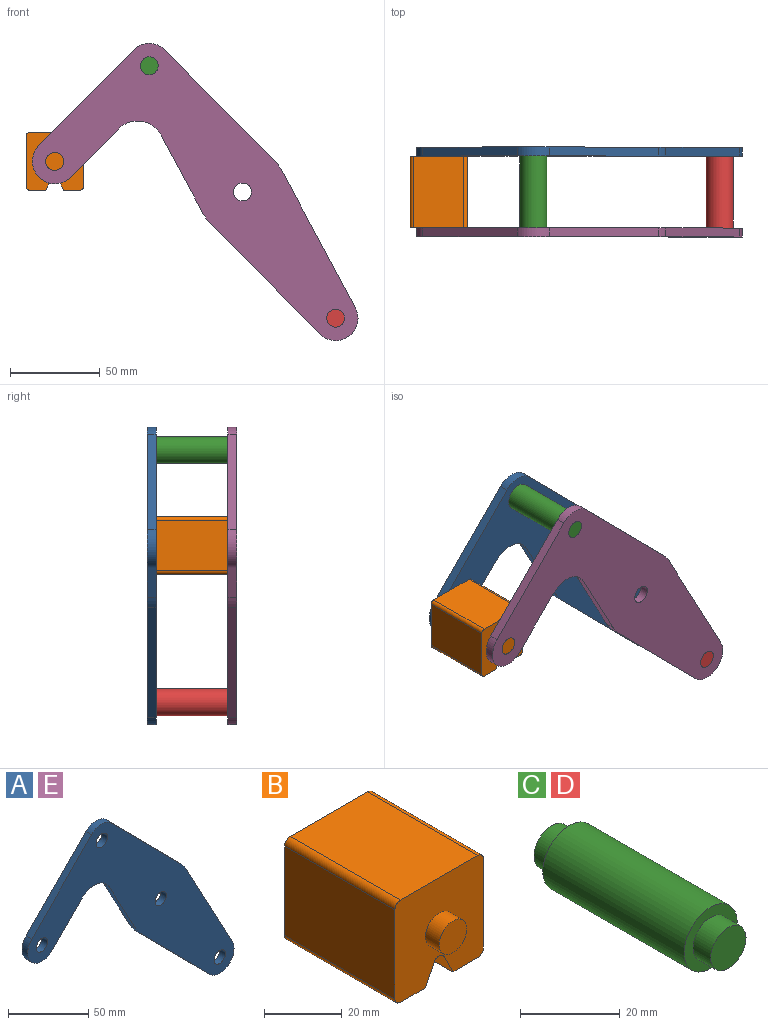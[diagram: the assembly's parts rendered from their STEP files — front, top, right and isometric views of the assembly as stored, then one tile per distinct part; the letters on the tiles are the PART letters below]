
ASSEMBLY  parts=5 mates=3
PART A: 18 faces, bbox 181.7x5x165.8 mm
  f0: plane 43.49x23.35mm, normal (-0.88,0,-0.47), area 246.8mm2, adj f1,f14,f16,f17
  f1: cylinder r=25mm len=5.75mm, axis (0,1,0), area 35.8mm2, adj f0,f2,f16,f17
  f2: plane 61.6x60.87mm, normal (-0.71,0,-0.7), area 433mm2, adj f1,f3,f16,f17
  f3: cylinder r=12.5mm len=21.39mm, axis (0,1,0), area 178.4mm2, adj f2,f4,f16,f17
  f4: plane 76.3x40.96mm, normal (0.88,0,0.47), area 433mm2, adj f3,f5,f16,f17
  f5: cylinder r=25mm len=5.75mm, axis (0,1,0), area 35.8mm2, adj f4,f6,f16,f17
  f6: plane 61.6x60.87mm, normal (0.71,0,0.7), area 433mm2, adj f5,f7,f16,f17
  f7: cylinder r=12.5mm len=17.78mm, axis (0,1,0), area 98.9mm2, adj f6,f8,f16,f17
  f8: plane 53.35x52.71mm, normal (-0.71,0,0.7), area 375mm2, adj f7,f9,f16,f17
  f9: cylinder r=12.5mm len=21.39mm, axis (0,1,0), area 196.3mm2, adj f8,f10,f16,f17
  f10: plane 26.86x26.54mm, normal (0.71,0,-0.7), area 188.8mm2, adj f9,f14,f16,f17
  f11: cylinder r=5mm len=10mm, axis (0,1,0), area 157.1mm2, adj f16,f17
  f12: cylinder r=5mm len=10mm, axis (0,1,0), area 157.1mm2, adj f16,f17
  f13: cylinder r=5mm len=10mm, axis (0,1,0), area 157.1mm2, adj f16,f17
  f14: cylinder r=15mm len=23.89mm, axis (0,1,0), area 140.2mm2, adj f0,f10,f16,f17
  f15: cylinder r=5mm len=10mm, axis (0,1,0), area 157.1mm2, adj f16,f17
  f16: plane 181.66x165.78mm, normal (0,-1,0), area 8710.1mm2, adj f0,f1,f2,f3,f4,f5,f6,f7
  f17: plane 181.66x165.78mm, normal (0,1,0), area 8710.1mm2, adj f0,f1,f2,f3,f4,f5,f6,f7
PART B: 18 faces, bbox 32.1x50x32.1 mm
  f0: plane 40x28.08mm, normal (1,0,0), area 1123.1mm2, adj f4,f10,f13,f14
  f1: plane 40x9.04mm, normal (0,0,-1), area 361.6mm2, adj f2,f4,f10,f14
  f2: plane 40x6.42mm, normal (-0.89,0,-0.45), area 287.2mm2, adj f1,f4,f10,f15
  f3: plane 40x6.42mm, normal (0.89,0,-0.45), area 287.2mm2, adj f4,f5,f10,f15
  f4: plane 32.08x32.08mm, normal (0,-1,0), area 900.6mm2, adj f0,f1,f2,f3,f5,f6,f7,f9
  f5: plane 40x9.04mm, normal (0,0,-1), area 361.6mm2, adj f3,f4,f10,f16
  f6: plane 40x28.08mm, normal (0,0,1), area 1123.1mm2, adj f4,f10,f13,f17
  f7: plane 40x28.08mm, normal (-1,0,0), area 1123.1mm2, adj f4,f10,f16,f17
  f8: plane 10x10mm, normal (0,-1,0), area 78.5mm2, adj f9
  f9: cylinder r=5mm len=10mm, axis (0,1,0), area 157.1mm2, adj f4,f8
  f10: plane 32.08x32.08mm, normal (0,1,0), area 900.6mm2, adj f0,f1,f2,f3,f5,f6,f7,f12
  f11: plane 10x10mm, normal (0,1,0), area 78.5mm2, adj f12
  f12: cylinder r=5mm len=10mm, axis (0,-1,0), area 157.1mm2, adj f10,f11
  f13: cylinder r=2mm len=40mm, axis (0,1,0), area 125.7mm2, adj f0,f4,f6,f10
  f14: cylinder r=2mm len=40mm, axis (0,-1,0), area 125.7mm2, adj f0,f1,f4,f10
  f15: cylinder r=2mm len=40mm, axis (0,1,0), area 177.1mm2, adj f2,f3,f4,f10
  f16: cylinder r=2mm len=40mm, axis (0,1,0), area 125.7mm2, adj f4,f5,f7,f10
  f17: cylinder r=2mm len=40mm, axis (0,-1,0), area 125.7mm2, adj f4,f6,f7,f10
PART C: 7 faces, bbox 15x50x15 mm
  f0: cylinder r=7.5mm len=40mm, axis (0,-1,0), area 1885mm2, adj f2,f5
  f1: cylinder r=5mm len=10mm, axis (0,1,0), area 157.1mm2, adj f2,f3
  f2: plane 15x15mm, normal (0,-1,0), area 98.2mm2, adj f0,f1
  f3: plane 10x10mm, normal (0,-1,0), area 78.5mm2, adj f1
  f4: cylinder r=5mm len=10mm, axis (0,-1,0), area 157.1mm2, adj f5,f6
  f5: plane 15x15mm, normal (0,1,0), area 98.2mm2, adj f0,f4
  f6: plane 10x10mm, normal (0,1,0), area 78.5mm2, adj f4
PART D: same geometry as C
PART E: same geometry as A
PLACE A t=(0,25,0)mm
PLACE B t=(0,-20,0)mm
PLACE C t=(0,-20,0)mm
PLACE D t=(103.95,-20,-140.78)mm
PLACE E t=(0,-20,0)mm fixed
MATE revolute E.f9 <-> B.f9  axis (0,1,0) through (-104.69,-20,17.04)mm
MATE fastened D.f0 <-> E.f3  axis (0,-1,0) through (51.98,-20,-70.39)mm
MATE fastened A.f7 <-> C.f0  axis (0,-1,0) through (-51.98,20,70.39)mm
